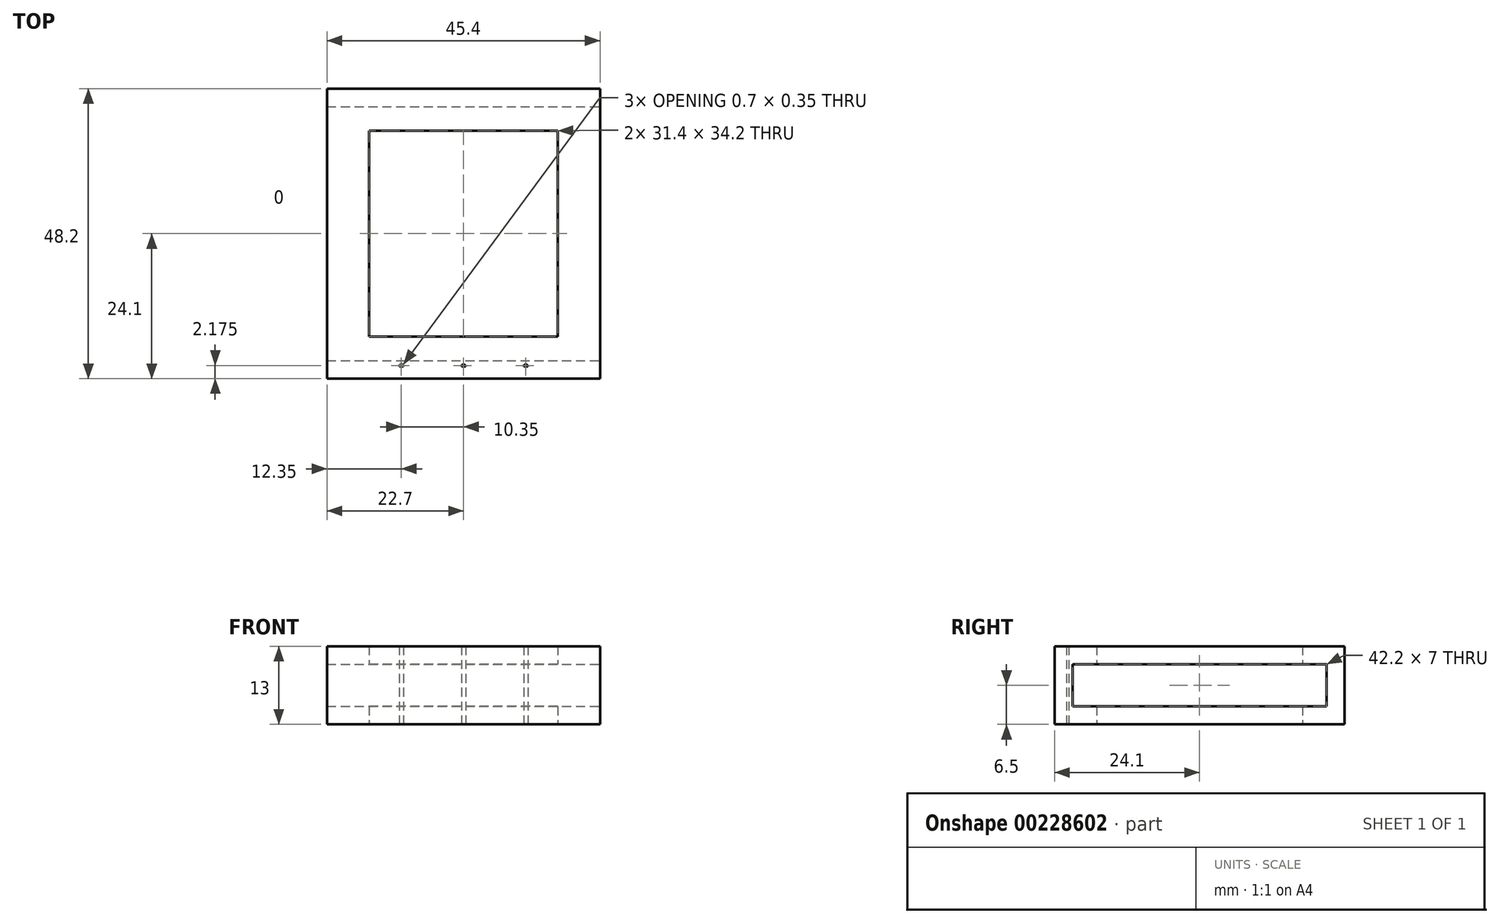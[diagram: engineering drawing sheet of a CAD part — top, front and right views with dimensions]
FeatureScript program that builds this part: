
annotation { "Feature Type Name" : "Feature", "Feature Type Description" : "" }
export const myFeature = defineFeature(function(context is Context, id is Id, definition is map)
    precondition{}
    {
        {
            var Q0;
            Q0=qCreatedBy(makeId("Top.planeOp"),FACE);
            var sketch = newSketch(context, id + "F0", { "sketchPlane" : qUnion([Q0])});
            skLineSegment(sketch, "E0.bottom", {"start": v(-20.7, 22.1) * mm, "end": v(20.7, 22.1) * mm});
            skLineSegment(sketch, "E0.top", {"start": v(-20.7, -22.1) * mm, "end": v(20.7, -22.1) * mm});
            skLineSegment(sketch, "E0.left", {"start": v(-20.7, 22.1) * mm, "end": v(-20.7, -22.1) * mm});
            skLineSegment(sketch, "E0.right", {"start": v(20.7, 22.1) * mm, "end": v(20.7, -22.1) * mm});
            skPoint(sketch, "E0.middle", {"position": v(0, 0) * mm});
            skLineSegment(sketch, "E1.bottom", {"start": v(-15.7, 17.1) * mm, "end": v(15.7, 17.1) * mm});
            skLineSegment(sketch, "E1.top", {"start": v(-15.7, -17.1) * mm, "end": v(15.7, -17.1) * mm});
            skLineSegment(sketch, "E1.left", {"start": v(-15.7, 17.1) * mm, "end": v(-15.7, -17.1) * mm});
            skLineSegment(sketch, "E1.right", {"start": v(15.7, 17.1) * mm, "end": v(15.7, -17.1) * mm});
            skLineSegment(sketch, "E2.bottom", {"start": v(-22.7, 24.1) * mm, "end": v(22.7, 24.1) * mm});
            skLineSegment(sketch, "E2.top", {"start": v(-22.7, -24.1) * mm, "end": v(22.7, -24.1) * mm});
            skLineSegment(sketch, "E2.left", {"start": v(-22.7, 24.1) * mm, "end": v(-22.7, -24.1) * mm});
            skLineSegment(sketch, "E2.right", {"start": v(22.7, 24.1) * mm, "end": v(22.7, -24.1) * mm});
            skArc(sketch, "E3", {"start": v(-0.35, 22.1) * mm, "mid": v(0, 21.75) * mm, "end": v(0.35, 22.1) * mm});
            skArc(sketch, "E4", {"start": v(-10.7, 22.1) * mm, "mid": v(-10.35, 21.75) * mm, "end": v(-10, 22.1) * mm});
            skArc(sketch, "E5", {"start": v(10, 22.1) * mm, "mid": v(10.35, 21.75) * mm, "end": v(10.7, 22.1) * mm});
            skArc(sketch, "E6.MirrorCS", {"start": v(-10.7, -22.1) * mm, "mid": v(-10.35, -21.75) * mm, "end": v(-10, -22.1) * mm});
            skArc(sketch, "E7.MirrorCS", {"start": v(-0.35, -22.1) * mm, "mid": v(0, -21.75) * mm, "end": v(0.35, -22.1) * mm});
            skArc(sketch, "E8.MirrorCS", {"start": v(10, -22.1) * mm, "mid": v(10.35, -21.75) * mm, "end": v(10.7, -22.1) * mm});
            skSolve(sketch);
        }
        {
            var Q0;
            Q0=makeQuery(id+"F0.imprint","IMPRINT",FACE,{"disambiguationData":[TD([[makeQuery(id+"F0.imprint","IMPRINT",EDGE,{"derivedFrom":sQuery(id+"F0.wireOp",EDGE,"E0.bottom")}),-1.0]])]});
            var Q1;
            Q1=makeQuery(id+"F0.imprint","IMPRINT",FACE,{"disambiguationData":[TD([[makeQuery(id+"F0.imprint","IMPRINT",EDGE,{"derivedFrom":sQuery(id+"F0.wireOp",EDGE,"E0.bottom")}),1.0]])]});
            extrude(context, id + "F1", {"entities" : qUnion([Q0, Q1]), "depth" : 2 * mm});
        }
        {
            var Q0;
            Q0=makeQuery(id+"F0.imprint","IMPRINT",FACE,{"disambiguationData":[TD([[makeQuery(id+"F0.imprint","IMPRINT",EDGE,{"derivedFrom":sQuery(id+"F0.wireOp",EDGE,"E0.bottom")}),1.0]])]});
            extrude(context, id + "F2", {"entities" : qUnion([Q0]), "operationType" : NewBodyOperationType.ADD, "depth" : 13 * mm});
        }
        {
            var Q0;
            {var subQ0=sQuery(id+"F0.wireOp",EDGE,"E4");Q0=makeQuery(id+"F0.imprint","IMPRINT",FACE,{"disambiguationData":[TD([[makeQuery(id+"F0.imprint","IMPRINT",EDGE,{"derivedFrom":subQ0}),1.0]])]});}
            var Q1;
            {var subQ0=sQuery(id+"F0.wireOp",EDGE,"E3");Q1=makeQuery(id+"F0.imprint","IMPRINT",FACE,{"disambiguationData":[TD([[makeQuery(id+"F0.imprint","IMPRINT",EDGE,{"derivedFrom":subQ0}),1.0]])]});}
            var Q2;
            {var subQ0=sQuery(id+"F0.wireOp",EDGE,"E5");Q2=makeQuery(id+"F0.imprint","IMPRINT",FACE,{"disambiguationData":[TD([[makeQuery(id+"F0.imprint","IMPRINT",EDGE,{"derivedFrom":subQ0}),1.0]])]});}
            var Q3;
            {var subQ0=sQuery(id+"F0.wireOp",EDGE,"E6.MirrorCS");Q3=makeQuery(id+"F0.imprint","IMPRINT",FACE,{"disambiguationData":[TD([[makeQuery(id+"F0.imprint","IMPRINT",EDGE,{"derivedFrom":subQ0}),-1.0]])]});}
            var Q4;
            {var subQ0=sQuery(id+"F0.wireOp",EDGE,"E7.MirrorCS");Q4=makeQuery(id+"F0.imprint","IMPRINT",FACE,{"disambiguationData":[TD([[makeQuery(id+"F0.imprint","IMPRINT",EDGE,{"derivedFrom":subQ0}),-1.0]])]});}
            var Q5;
            {var subQ0=sQuery(id+"F0.wireOp",EDGE,"E8.MirrorCS");Q5=makeQuery(id+"F0.imprint","IMPRINT",FACE,{"disambiguationData":[TD([[makeQuery(id+"F0.imprint","IMPRINT",EDGE,{"derivedFrom":subQ0}),-1.0]])]});}
            extrude(context, id + "F3", {"entities" : qUnion([Q0, Q1, Q2, Q3, Q4, Q5]), "operationType" : NewBodyOperationType.ADD, "depth" : 13 * mm});
        }
        {
            var Q0;
            Q0=qCreatedBy(makeId("Right.planeOp"),FACE);
            var sketch = newSketch(context, id + "F4", { "sketchPlane" : qUnion([Q0])});
            skLineSegment(sketch, "E9.0", {"start": v(24.1, 13) * mm, "end": v(-24.1, 13) * mm});
            skSolve(sketch);
        }
        {
            var Q0;
            {var subQ0=sQuery(id+"F0.wireOp",EDGE,"E2.right");Q0=makeQuery(id+"F2.boolean.opBoolean","MERGE",FACE,{"derivedFrom":[makeQuery(id+"F1.opExtrude","SWEPT_FACE",FACE,{"disambiguationData":[OSD([subQ0])]}),makeQuery(id+"F2.opExtrude","SWEPT_FACE",FACE,{"disambiguationData":[OSD([subQ0])]})]});}
            var sketch = newSketch(context, id + "F5", { "sketchPlane" : qUnion([Q0])});
            skLineSegment(sketch, "E10", {"start": v(-24.1, 13) * mm, "end": v(24.1, 0) * mm, "construction": true});
            skLineSegment(sketch, "E11.bottom", {"start": v(-21.1, 3) * mm, "end": v(21.1, 3) * mm});
            skLineSegment(sketch, "E11.top", {"start": v(-21.1, 10) * mm, "end": v(21.1, 10) * mm});
            skLineSegment(sketch, "E11.left", {"start": v(-21.1, 3) * mm, "end": v(-21.1, 10) * mm});
            skLineSegment(sketch, "E11.right", {"start": v(21.1, 3) * mm, "end": v(21.1, 10) * mm});
            skPoint(sketch, "E11.middle", {"position": v(0, 6.5) * mm});
            skSolve(sketch);
        }
        {
            var Q0;
            Q0=makeQuery(id+"F5.imprint","IMPRINT",FACE,{"disambiguationData":[TD([[makeQuery(id+"F5.imprint","IMPRINT",EDGE,{"derivedFrom":sQuery(id+"F5.wireOp",EDGE,"E11.bottom")}),1.0]])]});
            extrude(context, id + "F6", {"entities" : qUnion([Q0]), "operationType" : NewBodyOperationType.REMOVE, "oppositeDirection" : true, "depth" : 80 * mm});
        }
    });
